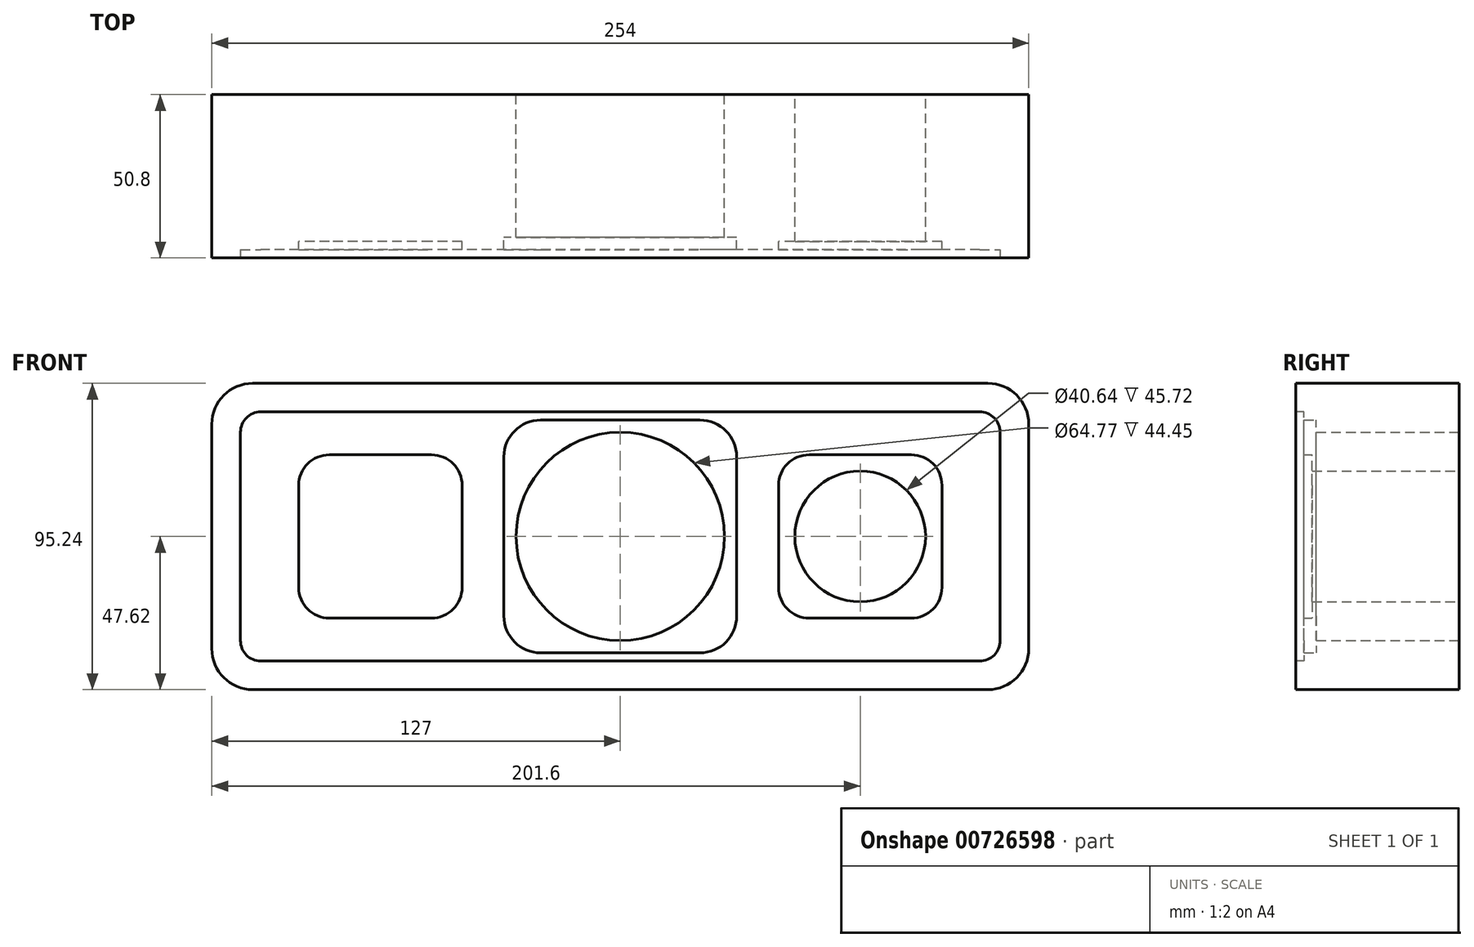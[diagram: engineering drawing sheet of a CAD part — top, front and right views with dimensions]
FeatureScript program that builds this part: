
annotation { "Feature Type Name" : "Feature", "Feature Type Description" : "" }
export const myFeature = defineFeature(function(context is Context, id is Id, definition is map)
    precondition{}
    {
        {
            var Q0;
            Q0=qCreatedBy(makeId("Front.planeOp"),FACE);
            var sketch = newSketch(context, id + "F0", { "sketchPlane" : qUnion([Q0])});
            skLineSegment(sketch, "E0.bottom", {"start": v(-114.3, 47.62) * mm, "end": v(114.3, 47.62) * mm});
            skLineSegment(sketch, "E0.top", {"start": v(-114.3, -47.63) * mm, "end": v(114.3, -47.63) * mm});
            skLineSegment(sketch, "E0.left", {"start": v(-127, 34.92) * mm, "end": v(-127, -34.93) * mm});
            skLineSegment(sketch, "E0.right", {"start": v(127, 34.92) * mm, "end": v(127, -34.93) * mm});
            skPoint(sketch, "E0.middle", {"position": v(0, 0) * mm});
            skCircle(sketch, "E1", {"center": v(-74.6, 0) * mm, "radius": 20.32 * mm});
            skPoint(sketch, "E2.visualSharp", {"position": v(-127, -47.63) * mm});
            skArc(sketch, "E2.filletArc", {"start": v(-127, -34.93) * mm, "mid": v(-123.28, -43.9) * mm, "end": v(-114.3, -47.63) * mm});
            skPoint(sketch, "E3.visualSharp", {"position": v(127, 47.62) * mm});
            skArc(sketch, "E3.filletArc", {"start": v(127, 34.92) * mm, "mid": v(123.28, 43.9) * mm, "end": v(114.3, 47.62) * mm});
            skPoint(sketch, "E4.visualSharp", {"position": v(127, -47.63) * mm});
            skArc(sketch, "E4.filletArc", {"start": v(114.3, -47.63) * mm, "mid": v(123.28, -43.9) * mm, "end": v(127, -34.93) * mm});
            skArc(sketch, "E5.filletArc", {"start": v(-114.3, 47.63) * mm, "mid": v(-123.28, 43.9) * mm, "end": v(-127, 34.92) * mm});
            skCircle(sketch, "E6", {"center": v(0, 0) * mm, "radius": 32.39 * mm});
            skCircle(sketch, "E7.MirrorC", {"center": v(74.6, 0) * mm, "radius": 20.32 * mm});
            skSolve(sketch);
        }
        {
            var Q0;
            Q0 = qSketchRegion(id + "F0", true);
            var Q1;
            Q1=makeQuery(id+"F0.imprint","IMPRINT",FACE,{"disambiguationData":[TD([[makeQuery(id+"F0.imprint","IMPRINT",EDGE,{"derivedFrom":sQuery(id+"F0.wireOp",EDGE,"E7.MirrorC")}),-1.0]])]});
            var Q2;
            Q2=makeQuery(id+"F0.imprint","IMPRINT",FACE,{"disambiguationData":[TD([[makeQuery(id+"F0.imprint","IMPRINT",EDGE,{"derivedFrom":sQuery(id+"F0.wireOp",EDGE,"E6")}),-1.0]])]});
            var Q3;
            Q3=makeQuery(id+"F0.imprint","IMPRINT",FACE,{"disambiguationData":[TD([[makeQuery(id+"F0.imprint","IMPRINT",EDGE,{"derivedFrom":sQuery(id+"F0.wireOp",EDGE,"E1")}),1.0]])]});
            extrude(context, id + "F1", {"entities" : qUnion([Q0, Q1, Q2, Q3]), "endBound" : BoundingType.SYMMETRIC, "depth" : 50.8 * mm, "offsetDistance" : 25.4 * mm});
        }
        {
            var Q0;
            Q0=makeQuery(id+"F1.opExtrude","CAP_FACE",FACE,{"disambiguationData":[OSD([sQuery(id+"F0.wireOp",EDGE,"E0.bottom"),sQuery(id+"F0.wireOp",EDGE,"E0.top"),sQuery(id+"F0.wireOp",EDGE,"E0.left"),sQuery(id+"F0.wireOp",EDGE,"E0.right"),sQuery(id+"F0.wireOp",EDGE,"E2.filletArc"),sQuery(id+"F0.wireOp",EDGE,"E3.filletArc"),sQuery(id+"F0.wireOp",EDGE,"E4.filletArc"),sQuery(id+"F0.wireOp",EDGE,"E5.filletArc")])],"isStart":false});
            var sketch = newSketch(context, id + "F2", { "sketchPlane" : qUnion([Q0])});
            skLineSegment(sketch, "E8.bottom", {"start": v(111.76, -38.73) * mm, "end": v(-111.76, -38.73) * mm});
            skLineSegment(sketch, "E8.top", {"start": v(111.76, 38.73) * mm, "end": v(-111.76, 38.73) * mm});
            skLineSegment(sketch, "E8.left", {"start": v(118.11, -32.38) * mm, "end": v(118.11, 32.38) * mm});
            skLineSegment(sketch, "E8.right", {"start": v(-118.11, -32.38) * mm, "end": v(-118.11, 32.38) * mm});
            skPoint(sketch, "E8.middle", {"position": v(0, 0) * mm});
            skPoint(sketch, "E9.visualSharp", {"position": v(-118.11, 38.73) * mm});
            skArc(sketch, "E9.filletArc", {"start": v(-111.76, 38.73) * mm, "mid": v(-116.25, 36.88) * mm, "end": v(-118.11, 32.38) * mm});
            skPoint(sketch, "E10.visualSharp", {"position": v(-118.11, -38.73) * mm});
            skArc(sketch, "E10.filletArc", {"start": v(-118.11, -32.38) * mm, "mid": v(-116.25, -36.88) * mm, "end": v(-111.76, -38.73) * mm});
            skPoint(sketch, "E11.visualSharp", {"position": v(118.11, -38.73) * mm});
            skArc(sketch, "E11.filletArc", {"start": v(111.76, -38.73) * mm, "mid": v(116.25, -36.88) * mm, "end": v(118.11, -32.38) * mm});
            skPoint(sketch, "E12.visualSharp", {"position": v(118.11, 38.73) * mm});
            skArc(sketch, "E12.filletArc", {"start": v(118.11, 32.38) * mm, "mid": v(116.25, 36.88) * mm, "end": v(111.76, 38.73) * mm});
            skSolve(sketch);
        }
        {
            var Q0;
            Q0 = qSketchRegion(id + "F2", true);
            extrude(context, id + "F3", {"entities" : qUnion([Q0]), "operationType" : NewBodyOperationType.REMOVE, "oppositeDirection" : true, "depth" : 2.54 * mm, "offsetDistance" : 25.4 * mm});
        }
        {
            var Q0;
            Q0=makeQuery(id+"F3.boolean.opBoolean","COPY",FACE,{"derivedFrom":makeQuery(id+"F3.opExtrude","CAP_FACE",FACE,{"disambiguationData":[OSD([sQuery(id+"F2.wireOp",EDGE,"E8.bottom"),sQuery(id+"F2.wireOp",EDGE,"E8.top"),sQuery(id+"F2.wireOp",EDGE,"E8.left"),sQuery(id+"F2.wireOp",EDGE,"E8.right"),sQuery(id+"F2.wireOp",EDGE,"E9.filletArc"),sQuery(id+"F2.wireOp",EDGE,"E10.filletArc"),sQuery(id+"F2.wireOp",EDGE,"E11.filletArc"),sQuery(id+"F2.wireOp",EDGE,"E12.filletArc")])],"isStart":false})});
            var sketch = newSketch(context, id + "F4", { "sketchPlane" : qUnion([Q0])});
            skLineSegment(sketch, "E13.bottom", {"start": v(-24.77, 36.2) * mm, "end": v(24.77, 36.2) * mm});
            skLineSegment(sketch, "E13.top", {"start": v(-24.77, -36.2) * mm, "end": v(24.77, -36.2) * mm});
            skLineSegment(sketch, "E13.left", {"start": v(-36.2, 24.76) * mm, "end": v(-36.2, -24.77) * mm});
            skLineSegment(sketch, "E13.right", {"start": v(36.2, 24.77) * mm, "end": v(36.2, -24.77) * mm});
            skPoint(sketch, "E13.middle", {"position": v(0, 0) * mm});
            skPoint(sketch, "E14.visualSharp", {"position": v(-36.2, 36.2) * mm});
            skArc(sketch, "E14.filletArc", {"start": v(-24.77, 36.2) * mm, "mid": v(-32.85, 32.85) * mm, "end": v(-36.2, 24.77) * mm});
            skPoint(sketch, "E15.visualSharp", {"position": v(36.2, 36.2) * mm});
            skArc(sketch, "E15.filletArc", {"start": v(36.2, 24.77) * mm, "mid": v(32.85, 32.85) * mm, "end": v(24.77, 36.2) * mm});
            skPoint(sketch, "E16.visualSharp", {"position": v(36.2, -36.2) * mm});
            skArc(sketch, "E16.filletArc", {"start": v(24.77, -36.2) * mm, "mid": v(32.85, -32.85) * mm, "end": v(36.2, -24.77) * mm});
            skPoint(sketch, "E17.visualSharp", {"position": v(-36.2, -36.2) * mm});
            skArc(sketch, "E17.filletArc", {"start": v(-36.2, -24.77) * mm, "mid": v(-32.85, -32.85) * mm, "end": v(-24.77, -36.2) * mm});
            skSolve(sketch);
        }
        {
            var Q0;
            Q0 = qSketchRegion(id + "F4", true);
            extrude(context, id + "F5", {"entities" : qUnion([Q0]), "operationType" : NewBodyOperationType.REMOVE, "oppositeDirection" : true, "depth" : 3.8 * mm, "offsetDistance" : 25.4 * mm, "hasDraft" : true, "draftAngle" : 0.25 * degree});
        }
        {
            var Q0;
            Q0=makeQuery(id+"F3.boolean.opBoolean","COPY",FACE,{"derivedFrom":makeQuery(id+"F3.opExtrude","CAP_FACE",FACE,{"disambiguationData":[OSD([sQuery(id+"F2.wireOp",EDGE,"E8.bottom"),sQuery(id+"F2.wireOp",EDGE,"E8.top"),sQuery(id+"F2.wireOp",EDGE,"E8.left"),sQuery(id+"F2.wireOp",EDGE,"E8.right"),sQuery(id+"F2.wireOp",EDGE,"E9.filletArc"),sQuery(id+"F2.wireOp",EDGE,"E10.filletArc"),sQuery(id+"F2.wireOp",EDGE,"E11.filletArc"),sQuery(id+"F2.wireOp",EDGE,"E12.filletArc")])],"isStart":false})});
            var sketch = newSketch(context, id + "F6", { "sketchPlane" : qUnion([Q0])});
            skLineSegment(sketch, "E18.bottom", {"start": v(-90.47, 25.4) * mm, "end": v(-58.72, 25.4) * mm});
            skLineSegment(sketch, "E18.top", {"start": v(-90.47, -25.4) * mm, "end": v(-58.72, -25.4) * mm});
            skLineSegment(sketch, "E18.left", {"start": v(-100, 15.87) * mm, "end": v(-100, -15.88) * mm});
            skLineSegment(sketch, "E18.right", {"start": v(-49.2, 15.87) * mm, "end": v(-49.2, -15.88) * mm});
            skPoint(sketch, "E18.middle", {"position": v(-74.6, 0) * mm});
            skPoint(sketch, "E19.visualSharp", {"position": v(-100, 25.4) * mm});
            skArc(sketch, "E19.filletArc", {"start": v(-90.47, 25.4) * mm, "mid": v(-97.2, 22.61) * mm, "end": v(-100, 15.87) * mm});
            skPoint(sketch, "E20.visualSharp", {"position": v(-49.2, 25.4) * mm});
            skArc(sketch, "E20.filletArc", {"start": v(-49.2, 15.87) * mm, "mid": v(-51.99, 22.61) * mm, "end": v(-58.72, 25.4) * mm});
            skPoint(sketch, "E21.visualSharp", {"position": v(-49.2, -25.4) * mm});
            skArc(sketch, "E21.filletArc", {"start": v(-58.72, -25.4) * mm, "mid": v(-51.99, -22.61) * mm, "end": v(-49.2, -15.88) * mm});
            skPoint(sketch, "E22.visualSharp", {"position": v(-100, -25.4) * mm});
            skArc(sketch, "E22.filletArc", {"start": v(-100, -15.88) * mm, "mid": v(-97.2, -22.61) * mm, "end": v(-90.47, -25.4) * mm});
            skLineSegment(sketch, "E23.MirrorCS", {"start": v(90.47, 25.4) * mm, "end": v(58.72, 25.4) * mm});
            skArc(sketch, "E24.MirrorCS", {"start": v(49.2, 15.87) * mm, "mid": v(51.99, 22.61) * mm, "end": v(58.72, 25.4) * mm});
            skLineSegment(sketch, "E25.MirrorCS", {"start": v(49.2, 15.87) * mm, "end": v(49.2, -15.88) * mm});
            skArc(sketch, "E26.MirrorCS", {"start": v(58.72, -25.4) * mm, "mid": v(51.99, -22.61) * mm, "end": v(49.2, -15.88) * mm});
            skLineSegment(sketch, "E27.MirrorCS", {"start": v(90.47, -25.4) * mm, "end": v(58.72, -25.4) * mm});
            skArc(sketch, "E28.MirrorCS", {"start": v(100, -15.88) * mm, "mid": v(97.2, -22.61) * mm, "end": v(90.47, -25.4) * mm});
            skLineSegment(sketch, "E29.MirrorCS", {"start": v(100, 15.87) * mm, "end": v(100, -15.88) * mm});
            skArc(sketch, "E30.MirrorCS", {"start": v(90.47, 25.4) * mm, "mid": v(97.2, 22.61) * mm, "end": v(100, 15.87) * mm});
            skSolve(sketch);
        }
        {
            var Q0;
            Q0 = qSketchRegion(id + "F6", true);
            extrude(context, id + "F7", {"entities" : qUnion([Q0]), "operationType" : NewBodyOperationType.REMOVE, "oppositeDirection" : true, "depth" : 2.54 * mm, "offsetDistance" : 25.4 * mm, "hasDraft" : true, "draftAngle" : 0.25 * degree});
        }
    });
